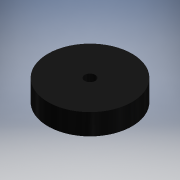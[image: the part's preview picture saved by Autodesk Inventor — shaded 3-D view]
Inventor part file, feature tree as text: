
AUTODESK INVENTOR PART (.ipt)
format: ipt  version: 2017 SP1 (Build 210196100, 196)  size: 95,744 bytes
history: native  units: in
note: dims shown in document units (in); Inventor stores cm internally (conversion verified against a paired STEP export)
features: extrude x1, sketch x1
ambient origin geometry x8: Origin, YZ Plane, XZ Plane, XY Plane, X Axis, Y Axis, Z Axis, Center Point
bodies: Solid1 (feature_tree)
feature tree (2):
  extrude  "Extrusion1"  Depth=1.0in
  sketch  "Sketch1"  dims[d0=0.5in d1=4.0in d2=1.0in d3=0.0in]
